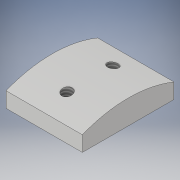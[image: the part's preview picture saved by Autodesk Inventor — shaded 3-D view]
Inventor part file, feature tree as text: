
AUTODESK INVENTOR PART (.ipt)
format: ipt  version: 2017 (Build 210142000, 142)  size: 116,224 bytes
history: native  units: in
note: dims shown in document units (in); Inventor stores cm internally (conversion verified against a paired STEP export)
features: sketch x2, extrude x1, hole x1, projected_geometry x1
ambient origin geometry x8: Origin, YZ Plane, XZ Plane, XY Plane, X Axis, Y Axis, Z Axis, Center Point
bodies: Solid1 (feature_tree)
feature tree (5):
  extrude  "Extrusion1"  Depth=0.125in
  hole  "Hole1"  [1 undecoded]
  sketch  "Sketch1"  dims[d0=0.75in d4=0.125in]
  sketch  "Sketch2"  dims[d6=1.0in d7=0.75in d8=0.625in d9=0.0in d10=0.625in d11=0.3125in d12=0.3125in d13=0.375in d14=0.75in d15=0.1875in d16=0.085in d17=0.224in d18=0.375in d19=0.25in d20=0.5635in d21=0.25in d22=0.8108in d23=0.125in]
  projected_geometry  "Projected Loop1"
note: 1 required parameter value undecoded (feature->parameter linkage not recoverable at this tier; creation-order binding heuristic only, values carry confidence <= 0.55)
